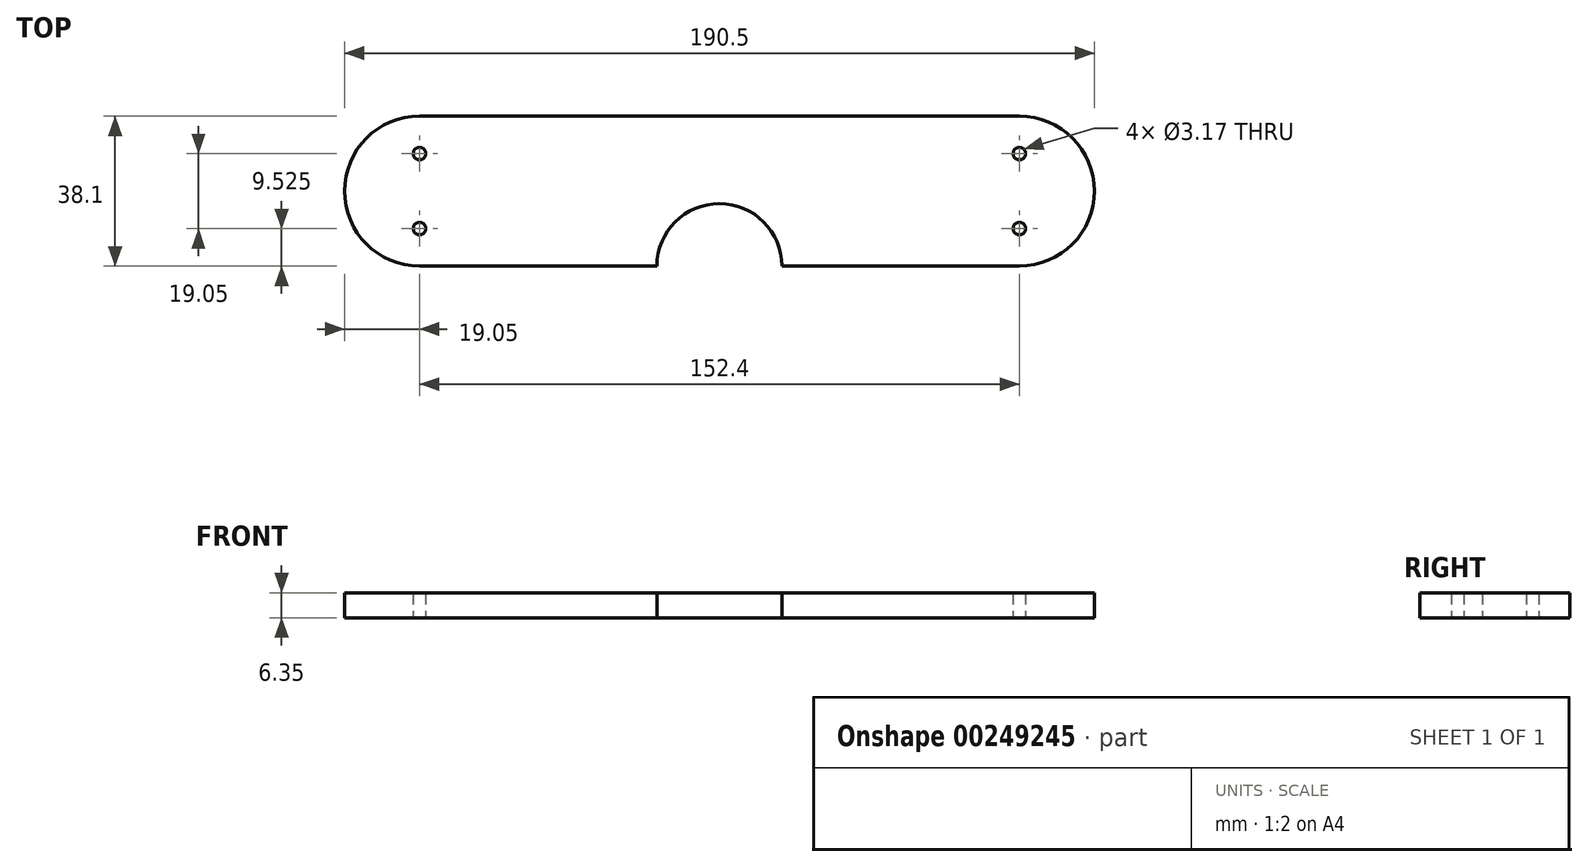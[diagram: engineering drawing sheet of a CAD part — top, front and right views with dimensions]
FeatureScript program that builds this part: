
annotation { "Feature Type Name" : "Feature", "Feature Type Description" : "" }
export const myFeature = defineFeature(function(context is Context, id is Id, definition is map)
    precondition{}
    {
        {
            var Q0;
            Q0=qCreatedBy(makeId("Top.planeOp"),FACE);
            var sketch = newSketch(context, id + "F0", { "sketchPlane" : qUnion([Q0])});
            skLineSegment(sketch, "E0", {"start": v(0, 0) * mm, "end": v(152.4, 0) * mm});
            skArc(sketch, "E1", {"start": v(0, 0) * mm, "mid": v(-19.05, -19.05) * mm, "end": v(0, -38.1) * mm});
            skLineSegment(sketch, "E2", {"start": v(0, -38.1) * mm, "end": v(60.33, -38.1) * mm});
            skArc(sketch, "E3", {"start": v(92.08, -38.1) * mm, "mid": v(76.2, -22.23) * mm, "end": v(60.33, -38.1) * mm});
            skLineSegment(sketch, "E4", {"start": v(92.08, -38.1) * mm, "end": v(152.4, -38.1) * mm});
            skArc(sketch, "E5", {"start": v(152.4, -38.1) * mm, "mid": v(171.45, -19.05) * mm, "end": v(152.4, 0) * mm});
            skCircle(sketch, "E6", {"center": v(0, -28.58) * mm, "radius": 1.59 * mm});
            skCircle(sketch, "E7", {"center": v(0, -9.53) * mm, "radius": 1.59 * mm});
            skCircle(sketch, "E8", {"center": v(152.4, -28.58) * mm, "radius": 1.59 * mm});
            skCircle(sketch, "E9", {"center": v(152.4, -9.52) * mm, "radius": 1.59 * mm});
            skSolve(sketch);
        }
        {
            var Q0;
            Q0=makeQuery(id+"F0.imprint","IMPRINT",FACE,{"disambiguationData":[TD([[makeQuery(id+"F0.imprint","IMPRINT",EDGE,{"derivedFrom":sQuery(id+"F0.wireOp",EDGE,"E0")}),-1.0]])]});
            extrude(context, id + "F1", {"entities" : qUnion([Q0]), "depth" : 6.35 * mm});
        }
    });
